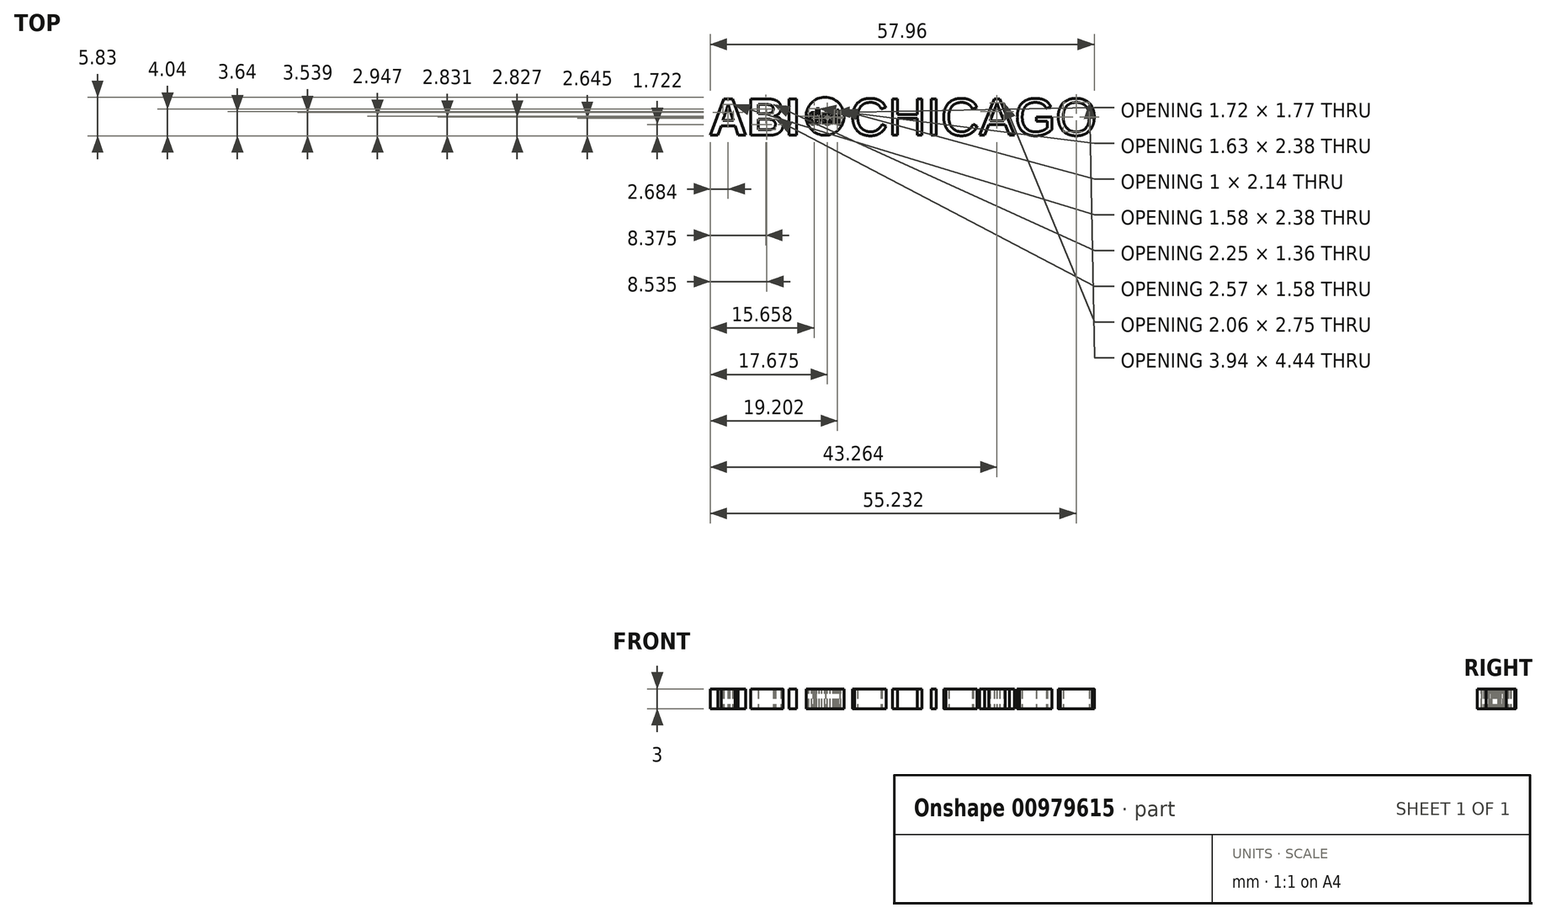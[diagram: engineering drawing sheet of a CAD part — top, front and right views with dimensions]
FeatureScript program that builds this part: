
annotation { "Feature Type Name" : "Feature", "Feature Type Description" : "" }
export const myFeature = defineFeature(function(context is Context, id is Id, definition is map)
    precondition{}
    {
        {
            var Q0;
            Q0=qCreatedBy(makeId("Top.planeOp"),FACE);
            var sketch = newSketch(context, id + "F0", { "sketchPlane" : qUnion([Q0])});
            skText(sketch, "E0", { "text": "ABI", "fontName": "Arimo-Bold.ttf"});
            skCircle(sketch, "E1", {"center": v(3.75, 2.87) * mm, "radius": 2.88 * mm});
            skPoint(sketch, "E2", {"position": v(-13.77, 2.88) * mm});
            skText(sketch, "E3", { "text": "CHICAGO", "fontName": "Arimo-Regular.ttf"});
            const initialGuessF0  = {"E0": [-0.01377, 0, 1, 0, 0.00575], "E3": [0.0075, 0, 1, 0, 0.00575]};
            skSetInitialGuess(sketch, initialGuessF0);
            skSolve(sketch);
        }
        {
            var Q0;
            Q0 = qSketchRegion(id + "F0", true);
            extrude(context, id + "F1", {"entities" : qUnion([Q0]), "depth" : 3 * mm, "offsetDistance" : 25 * mm});
        }
        {
            var Q0;
            Q0=makeQuery(id+"F1.opExtrude","CAP_FACE",FACE,{"disambiguationData":[OSD([sQuery(id+"F0.wireOp",EDGE,"E1")])],"isStart":false});
            var sketch = newSketch(context, id + "F2", { "sketchPlane" : qUnion([Q0])});
            skText(sketch, "E4", { "text": "dot", "fontName": "Arimo-Bold.ttf"});
            skPoint(sketch, "E5", {"position": v(3.75, 2.87) * mm});
            const initialGuessF2  = {"E4": [0.00114, 0.00171, 1, 0, 0.00233]};
            skSetInitialGuess(sketch, initialGuessF2);
            skSolve(sketch);
        }
        {
            var Q0;
            Q0 = qSketchRegion(id + "F2", true);
            extrude(context, id + "F3", {"entities" : qUnion([Q0]), "operationType" : NewBodyOperationType.REMOVE, "endBound" : BoundingType.THROUGH_ALL, "oppositeDirection" : true, "depth" : 10 * mm, "offsetDistance" : 25 * mm});
        }
    });
